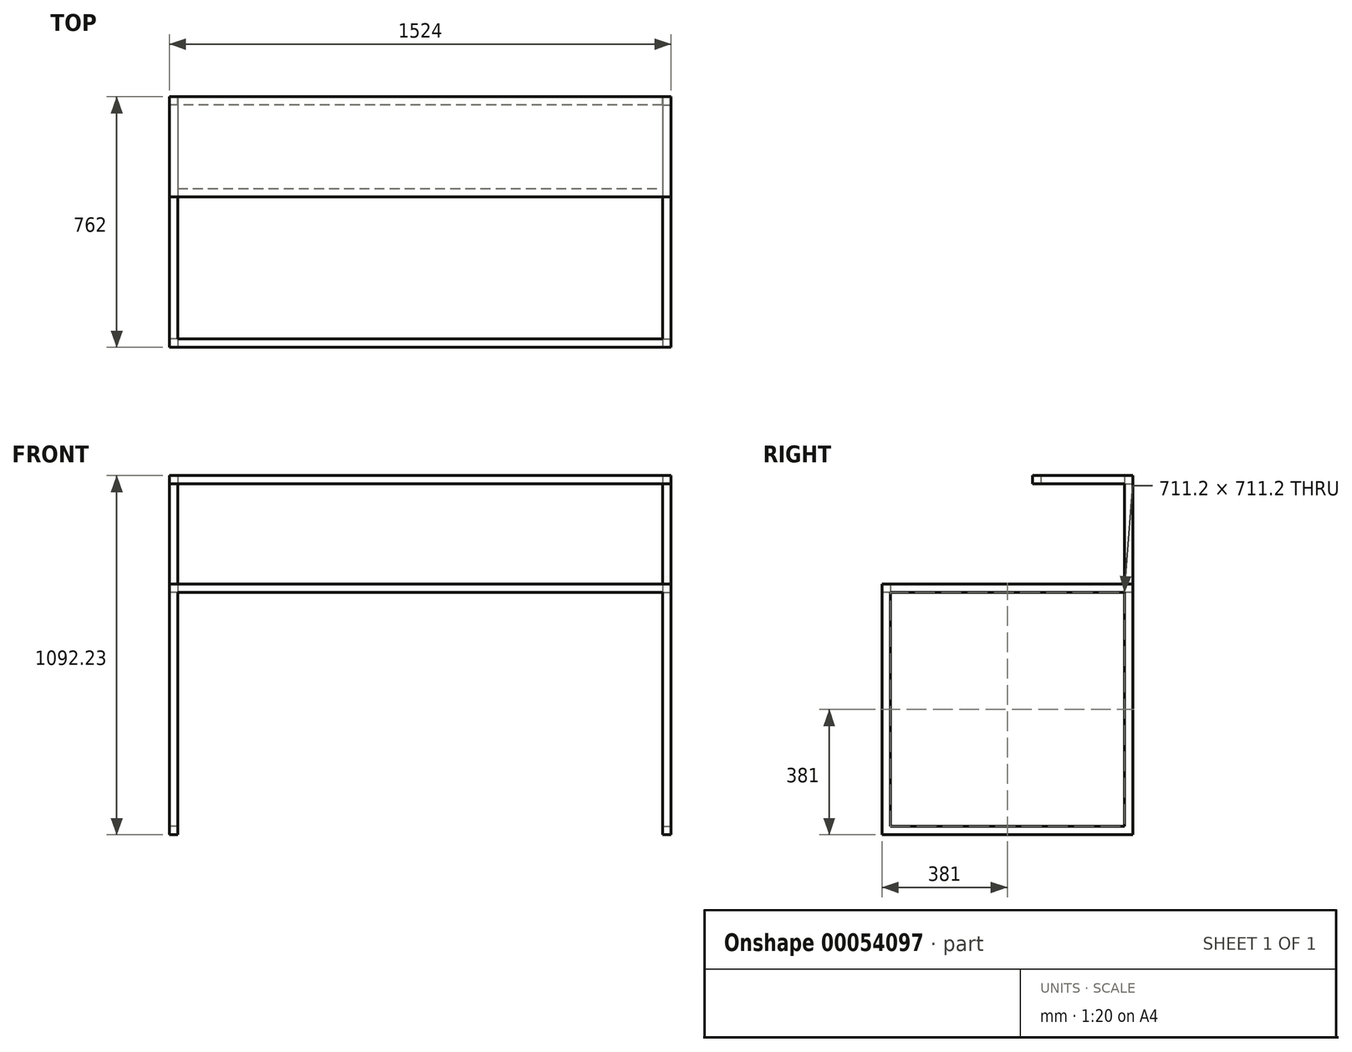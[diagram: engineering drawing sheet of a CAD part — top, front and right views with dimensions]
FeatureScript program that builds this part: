
annotation { "Feature Type Name" : "Feature", "Feature Type Description" : "" }
export const myFeature = defineFeature(function(context is Context, id is Id, definition is map)
    precondition{}
    {
        {
            var Q0;
            Q0=qCreatedBy(makeId("Top.planeOp"),FACE);
            var sketch = newSketch(context, id + "F0", { "sketchPlane" : qUnion([Q0])});
            skLineSegment(sketch, "E0.rect.bottom", {"start": v(762, 381) * mm, "end": v(-762, 381) * mm});
            skLineSegment(sketch, "E0.rect.top", {"start": v(762, -381) * mm, "end": v(-762, -381) * mm});
            skLineSegment(sketch, "E0.rect.left", {"start": v(762, 381) * mm, "end": v(762, -381) * mm});
            skLineSegment(sketch, "E0.rect.right", {"start": v(-762, 381) * mm, "end": v(-762, -381) * mm});
            skPoint(sketch, "E0.rect.middle", {"position": v(0, 0) * mm});
            skLineSegment(sketch, "E1.0", {"start": v(736.6, 355.6) * mm, "end": v(-736.6, 355.6) * mm});
            skLineSegment(sketch, "E1.1", {"start": v(736.6, 355.6) * mm, "end": v(736.6, -355.6) * mm});
            skLineSegment(sketch, "E1.2", {"start": v(736.6, -355.6) * mm, "end": v(-736.6, -355.6) * mm});
            skLineSegment(sketch, "E1.3", {"start": v(-736.6, 355.6) * mm, "end": v(-736.6, -355.6) * mm});
            skSolve(sketch);
        }
        {
            var Q0;
            Q0 = qSketchRegion(id + "F0", true);
            extrude(context, id + "F1", {"entities" : qUnion([Q0]), "depth" : 25.4 * mm});
        }
        {
            var Q0;
            Q0=makeQuery(id+"F1.opExtrude","CAP_FACE",FACE,{"disambiguationData":[OSD([sQuery(id+"F0.wireOp",EDGE,"E0.rect.bottom"),sQuery(id+"F0.wireOp",EDGE,"E0.rect.top"),sQuery(id+"F0.wireOp",EDGE,"E0.rect.left"),sQuery(id+"F0.wireOp",EDGE,"E0.rect.right"),sQuery(id+"F0.wireOp",EDGE,"E1.0"),sQuery(id+"F0.wireOp",EDGE,"E1.1"),sQuery(id+"F0.wireOp",EDGE,"E1.2"),sQuery(id+"F0.wireOp",EDGE,"E1.3")])],"isStart":true});
            var sketch = newSketch(context, id + "F2", { "sketchPlane" : qUnion([Q0])});
            skLineSegment(sketch, "E2.bottom", {"start": v(-736.6, 355.6) * mm, "end": v(-762, 355.6) * mm});
            skLineSegment(sketch, "E2.top", {"start": v(-736.6, 381) * mm, "end": v(-762, 381) * mm});
            skLineSegment(sketch, "E2.left", {"start": v(-736.6, 355.6) * mm, "end": v(-736.6, 381) * mm});
            skLineSegment(sketch, "E2.right", {"start": v(-762, 355.6) * mm, "end": v(-762, 381) * mm});
            skLineSegment(sketch, "E3.bottom", {"start": v(-736.6, -355.6) * mm, "end": v(-762, -355.6) * mm});
            skLineSegment(sketch, "E3.top", {"start": v(-736.6, -381) * mm, "end": v(-762, -381) * mm});
            skLineSegment(sketch, "E3.left", {"start": v(-736.6, -355.6) * mm, "end": v(-736.6, -381) * mm});
            skLineSegment(sketch, "E3.right", {"start": v(-762, -355.6) * mm, "end": v(-762, -381) * mm});
            skLineSegment(sketch, "E4.bottom", {"start": v(762, -381) * mm, "end": v(736.6, -381) * mm});
            skLineSegment(sketch, "E4.top", {"start": v(762, -355.6) * mm, "end": v(736.6, -355.6) * mm});
            skLineSegment(sketch, "E4.left", {"start": v(762, -381) * mm, "end": v(762, -355.6) * mm});
            skLineSegment(sketch, "E4.right", {"start": v(736.6, -381) * mm, "end": v(736.6, -355.6) * mm});
            skLineSegment(sketch, "E5.bottom", {"start": v(736.6, 355.6) * mm, "end": v(762, 355.6) * mm});
            skLineSegment(sketch, "E5.top", {"start": v(736.6, 381) * mm, "end": v(762, 381) * mm});
            skLineSegment(sketch, "E5.left", {"start": v(736.6, 355.6) * mm, "end": v(736.6, 381) * mm});
            skLineSegment(sketch, "E5.right", {"start": v(762, 355.6) * mm, "end": v(762, 381) * mm});
            skSolve(sketch);
        }
        {
            var Q0;
            Q0=makeQuery(id+"F2.imprint","IMPRINT",FACE,{"disambiguationData":[TD([[makeQuery(id+"F2.imprint","IMPRINT",EDGE,{"derivedFrom":sQuery(id+"F2.wireOp",EDGE,"E2.bottom")}),-1.0]])]});
            var Q1;
            Q1=makeQuery(id+"F2.imprint","IMPRINT",FACE,{"disambiguationData":[TD([[makeQuery(id+"F2.imprint","IMPRINT",EDGE,{"derivedFrom":sQuery(id+"F2.wireOp",EDGE,"E3.bottom")}),1.0]])]});
            var Q2;
            Q2=makeQuery(id+"F2.imprint","IMPRINT",FACE,{"disambiguationData":[TD([[makeQuery(id+"F2.imprint","IMPRINT",EDGE,{"derivedFrom":sQuery(id+"F2.wireOp",EDGE,"E4.bottom")}),-1.0]])]});
            var Q3;
            Q3=makeQuery(id+"F2.imprint","IMPRINT",FACE,{"disambiguationData":[TD([[makeQuery(id+"F2.imprint","IMPRINT",EDGE,{"derivedFrom":sQuery(id+"F2.wireOp",EDGE,"E5.bottom")}),1.0]])]});
            extrude(context, id + "F3", {"entities" : qUnion([Q0, Q1, Q2, Q3]), "operationType" : NewBodyOperationType.ADD, "depth" : 736.6 * mm});
        }
        {
            var Q0;
            Q0=makeQuery(id+"F1.opExtrude","CAP_FACE",FACE,{"disambiguationData":[OSD([sQuery(id+"F0.wireOp",EDGE,"E0.rect.bottom"),sQuery(id+"F0.wireOp",EDGE,"E0.rect.top"),sQuery(id+"F0.wireOp",EDGE,"E0.rect.left"),sQuery(id+"F0.wireOp",EDGE,"E0.rect.right"),sQuery(id+"F0.wireOp",EDGE,"E1.0"),sQuery(id+"F0.wireOp",EDGE,"E1.1"),sQuery(id+"F0.wireOp",EDGE,"E1.2"),sQuery(id+"F0.wireOp",EDGE,"E1.3")])],"isStart":false});
            var sketch = newSketch(context, id + "F4", { "sketchPlane" : qUnion([Q0])});
            skLineSegment(sketch, "E6.bottom", {"start": v(-736.6, 355.6) * mm, "end": v(-762, 355.6) * mm});
            skLineSegment(sketch, "E6.top", {"start": v(-736.6, 381) * mm, "end": v(-762, 381) * mm});
            skLineSegment(sketch, "E6.left", {"start": v(-736.6, 355.6) * mm, "end": v(-736.6, 381) * mm});
            skLineSegment(sketch, "E6.right", {"start": v(-762, 355.6) * mm, "end": v(-762, 381) * mm});
            skLineSegment(sketch, "E7.bottom", {"start": v(736.6, 355.6) * mm, "end": v(762, 355.6) * mm});
            skLineSegment(sketch, "E7.top", {"start": v(736.6, 381) * mm, "end": v(762, 381) * mm});
            skLineSegment(sketch, "E7.left", {"start": v(736.6, 355.6) * mm, "end": v(736.6, 381) * mm});
            skLineSegment(sketch, "E7.right", {"start": v(762, 355.6) * mm, "end": v(762, 381) * mm});
            skSolve(sketch);
        }
        {
            var Q0;
            Q0=makeQuery(id+"F4.imprint","IMPRINT",FACE,{"disambiguationData":[TD([[makeQuery(id+"F4.imprint","IMPRINT",EDGE,{"derivedFrom":sQuery(id+"F4.wireOp",EDGE,"E7.bottom")}),1.0]])]});
            var Q1;
            Q1=makeQuery(id+"F4.imprint","IMPRINT",FACE,{"disambiguationData":[TD([[makeQuery(id+"F4.imprint","IMPRINT",EDGE,{"derivedFrom":sQuery(id+"F4.wireOp",EDGE,"E6.bottom")}),-1.0]])]});
            var Q2;
            Q2=makeQuery(id+"F4.imprint","IMPRINT",FACE,{"disambiguationData":[TD([[makeQuery(id+"F4.imprint","IMPRINT",EDGE,{"derivedFrom":sQuery(id+"F4.wireOp",EDGE,"a08b17ff-189d-42e0-89d5-0d836113f8d2.bottom")}),-1.0]])]});
            var Q3;
            Q3=makeQuery(id+"F4.imprint","IMPRINT",FACE,{"disambiguationData":[TD([[makeQuery(id+"F4.imprint","IMPRINT",EDGE,{"derivedFrom":sQuery(id+"F4.wireOp",EDGE,"f9240952-c8aa-4458-8341-3ee3489270d4.bottom")}),-1.0]])]});
            extrude(context, id + "F5", {"entities" : qUnion([Q0, Q1, Q2, Q3]), "operationType" : NewBodyOperationType.ADD, "depth" : 304.8 * mm});
        }
        {
            var Q0;
            Q0=makeQuery(id+"F5.opExtrude","CAP_FACE",FACE,{"disambiguationData":[OSD([sQuery(id+"F4.wireOp",EDGE,"E6.bottom"),sQuery(id+"F4.wireOp",EDGE,"E6.top"),sQuery(id+"F4.wireOp",EDGE,"E6.left"),sQuery(id+"F4.wireOp",EDGE,"E6.right")])],"isStart":false});
            var sketch = newSketch(context, id + "F6", { "sketchPlane" : qUnion([Q0])});
            skLineSegment(sketch, "E8.bottom", {"start": v(-762, 381) * mm, "end": v(762, 381) * mm});
            skLineSegment(sketch, "E8.top", {"start": v(-762, 76.2) * mm, "end": v(762, 76.2) * mm});
            skLineSegment(sketch, "E8.left", {"start": v(-762, 381) * mm, "end": v(-762, 76.2) * mm});
            skLineSegment(sketch, "E8.right", {"start": v(762, 381) * mm, "end": v(762, 76.2) * mm});
            skLineSegment(sketch, "E9.bottom", {"start": v(-736.6, 355.6) * mm, "end": v(736.6, 355.6) * mm});
            skLineSegment(sketch, "E9.top", {"start": v(-736.6, 101.6) * mm, "end": v(736.6, 101.6) * mm});
            skLineSegment(sketch, "E9.left", {"start": v(-736.6, 355.6) * mm, "end": v(-736.6, 101.6) * mm});
            skLineSegment(sketch, "E9.right", {"start": v(736.6, 355.6) * mm, "end": v(736.6, 101.6) * mm});
            skSolve(sketch);
        }
        {
            var Q0;
            Q0 = qSketchRegion(id + "F6", true);
            extrude(context, id + "F7", {"entities" : qUnion([Q0]), "operationType" : NewBodyOperationType.ADD, "depth" : 25.4 * mm});
        }
        {
            var Q0;
            Q0=makeQuery(id+"F5.boolean.opBoolean","MERGE",FACE,{"derivedFrom":[makeQuery(id+"F3.boolean.opBoolean","MERGE",FACE,{"derivedFrom":[makeQuery(id+"F1.opExtrude","SWEPT_FACE",FACE,{"disambiguationData":[OSD([sQuery(id+"F0.wireOp",EDGE,"E0.rect.left")])]}),makeQuery(id+"F3.opExtrude","SWEPT_FACE",FACE,{"disambiguationData":[OSD([sQuery(id+"F2.wireOp",EDGE,"E4.left")])]}),makeQuery(id+"F3.opExtrude","SWEPT_FACE",FACE,{"disambiguationData":[OSD([sQuery(id+"F2.wireOp",EDGE,"E5.right")])]})]}),makeQuery(id+"F5.opExtrude","SWEPT_FACE",FACE,{"disambiguationData":[OSD([sQuery(id+"F4.wireOp",EDGE,"E7.right")])]})]});
            var sketch = newSketch(context, id + "F8", { "sketchPlane" : qUnion([Q0])});
            skLineSegment(sketch, "E10.bottom", {"start": v(-381, -736.6) * mm, "end": v(381, -736.6) * mm});
            skLineSegment(sketch, "E10.top", {"start": v(-381, -711.2) * mm, "end": v(381, -711.2) * mm});
            skLineSegment(sketch, "E10.left", {"start": v(-381, -736.6) * mm, "end": v(-381, -711.2) * mm});
            skLineSegment(sketch, "E10.right", {"start": v(381, -736.6) * mm, "end": v(381, -711.2) * mm});
            skSolve(sketch);
        }
        {
            var Q0;
            {var subQ0=sQuery(id+"F8.wireOp",EDGE,"E10.bottom");var subQ1=sQuery(id+"F0.wireOp",EDGE,"E0.rect.left");var subQ2=makeQuery(id+"F3.opExtrude","SWEPT_EDGE",EDGE,{"disambiguationData":[OSD([subQ1,sQuery(id+"F2.wireOp",EDGE,"E4.top"),sQuery(id+"F2.wireOp",EDGE,"E4.left")])]});var subQ3=makeQuery(id+"F8.imprint","INTERSECT",VERTEX,{"derivedFrom":[subQ2,subQ0]});var subQ4=makeQuery(id+"F3.opExtrude","SWEPT_EDGE",EDGE,{"disambiguationData":[OSD([subQ1,sQuery(id+"F2.wireOp",EDGE,"E5.bottom"),sQuery(id+"F2.wireOp",EDGE,"E5.right")])]});var subQ5=makeQuery(id+"F8.imprint","INTERSECT",VERTEX,{"derivedFrom":[subQ4,subQ0]});Q0=makeQuery(id+"F8.imprint","IMPRINT",FACE,{"disambiguationData":[TD([[makeQuery(id+"F8.imprint","IMPRINT",EDGE,{"disambiguationData":[TD([[subQ3,1.0],[subQ5,-1.0]])],"derivedFrom":subQ0}),1.0]])]});}
            extrude(context, id + "F9", {"entities" : qUnion([Q0]), "operationType" : NewBodyOperationType.ADD, "oppositeDirection" : true, "depth" : 25.4 * mm});
        }
        {
            var Q0;
            Q0=makeQuery(id+"F7.boolean.opBoolean","MERGE",FACE,{"derivedFrom":[makeQuery(id+"F5.boolean.opBoolean","MERGE",FACE,{"derivedFrom":[makeQuery(id+"F3.boolean.opBoolean","MERGE",FACE,{"derivedFrom":[makeQuery(id+"F1.opExtrude","SWEPT_FACE",FACE,{"disambiguationData":[OSD([sQuery(id+"F0.wireOp",EDGE,"E0.rect.right")])]}),makeQuery(id+"F3.opExtrude","SWEPT_FACE",FACE,{"disambiguationData":[OSD([sQuery(id+"F2.wireOp",EDGE,"E2.right")])]}),makeQuery(id+"F3.opExtrude","SWEPT_FACE",FACE,{"disambiguationData":[OSD([sQuery(id+"F2.wireOp",EDGE,"E3.right")])]})]}),makeQuery(id+"F5.opExtrude","SWEPT_FACE",FACE,{"disambiguationData":[OSD([sQuery(id+"F4.wireOp",EDGE,"E6.right")])]})]}),makeQuery(id+"F7.opExtrude","SWEPT_FACE",FACE,{"disambiguationData":[OSD([sQuery(id+"F6.wireOp",EDGE,"E8.left")])]})]});
            var sketch = newSketch(context, id + "F10", { "sketchPlane" : qUnion([Q0])});
            skLineSegment(sketch, "E11.bottom", {"start": v(-381, -736.6) * mm, "end": v(381, -736.6) * mm});
            skLineSegment(sketch, "E11.top", {"start": v(-381, -711.2) * mm, "end": v(381, -711.2) * mm});
            skLineSegment(sketch, "E11.left", {"start": v(-381, -736.6) * mm, "end": v(-381, -711.2) * mm});
            skLineSegment(sketch, "E11.right", {"start": v(381, -736.6) * mm, "end": v(381, -711.2) * mm});
            skSolve(sketch);
        }
        {
            var Q0;
            {var subQ0=sQuery(id+"F10.wireOp",EDGE,"E11.bottom");var subQ1=sQuery(id+"F0.wireOp",EDGE,"E0.rect.right");var subQ2=makeQuery(id+"F3.opExtrude","SWEPT_EDGE",EDGE,{"disambiguationData":[OSD([subQ1,sQuery(id+"F2.wireOp",EDGE,"E2.bottom"),sQuery(id+"F2.wireOp",EDGE,"E2.right")])]});var subQ3=makeQuery(id+"F10.imprint","INTERSECT",VERTEX,{"derivedFrom":[subQ2,subQ0]});Q0=makeQuery(id+"F10.imprint","IMPRINT",FACE,{"disambiguationData":[TD([[makeQuery(id+"F10.imprint","IMPRINT",EDGE,{"disambiguationData":[TD([[subQ3,1.0]])],"derivedFrom":subQ0}),1.0]])]});}
            extrude(context, id + "F11", {"entities" : qUnion([Q0]), "operationType" : NewBodyOperationType.ADD, "oppositeDirection" : true, "depth" : 25.4 * mm});
        }
        {
            var Q0;
            {var subQ0=sQuery(id+"F0.wireOp",EDGE,"E1.3");var subQ1=sQuery(id+"F0.wireOp",EDGE,"E1.2");var subQ2=sQuery(id+"F0.wireOp",EDGE,"E1.1");var subQ3=sQuery(id+"F0.wireOp",EDGE,"E1.0");var subQ4=sQuery(id+"F0.wireOp",EDGE,"E0.rect.right");var subQ5=sQuery(id+"F0.wireOp",EDGE,"E0.rect.left");var subQ6=sQuery(id+"F0.wireOp",EDGE,"E0.rect.top");var subQ7=makeQuery(id+"F1.opExtrude","CAP_FACE",FACE,{"disambiguationData":[OSD([sQuery(id+"F0.wireOp",EDGE,"E0.rect.bottom"),subQ6,subQ5,subQ4,subQ3,subQ2,subQ1,subQ0])],"isStart":false});Q0=makeQuery(id+"F5.boolean.opBoolean","SPLIT",FACE,{"disambiguationData":[TD([makeQuery(id+"F1.opExtrude","SWEPT_FACE",FACE,{"disambiguationData":[OSD([subQ6])]})])],"derivedFrom":subQ7});}
            var sketch = newSketch(context, id + "F12", { "sketchPlane" : qUnion([Q0])});
            skLineSegment(sketch, "E12.bottom", {"start": v(-762, -381) * mm, "end": v(762, -381) * mm});
            skLineSegment(sketch, "E12.top", {"start": v(-762, 381) * mm, "end": v(762, 381) * mm});
            skLineSegment(sketch, "E12.left", {"start": v(-762, -381) * mm, "end": v(-762, 381) * mm});
            skLineSegment(sketch, "E12.right", {"start": v(762, -381) * mm, "end": v(762, 381) * mm});
            skLineSegment(sketch, "E13.bottom", {"start": v(762, 381) * mm, "end": v(736.6, 381) * mm});
            skLineSegment(sketch, "E13.top", {"start": v(762, 355.6) * mm, "end": v(736.6, 355.6) * mm});
            skLineSegment(sketch, "E13.left", {"start": v(762, 381) * mm, "end": v(762, 355.6) * mm});
            skLineSegment(sketch, "E13.right", {"start": v(736.6, 381) * mm, "end": v(736.6, 355.6) * mm});
            skLineSegment(sketch, "E14.bottom", {"start": v(-762, 381) * mm, "end": v(-736.6, 381) * mm});
            skLineSegment(sketch, "E14.top", {"start": v(-762, 355.6) * mm, "end": v(-736.6, 355.6) * mm});
            skLineSegment(sketch, "E14.left", {"start": v(-762, 381) * mm, "end": v(-762, 355.6) * mm});
            skLineSegment(sketch, "E14.right", {"start": v(-736.6, 381) * mm, "end": v(-736.6, 355.6) * mm});
            skSolve(sketch);
        }
        {
            var Q0;
            Q0=makeQuery(id+"F12.imprint","IMPRINT",FACE,{"disambiguationData":[TD([[makeQuery(id+"F12.imprint","IMPRINT",EDGE,{"derivedFrom":sQuery(id+"F12.wireOp",EDGE,"E12.top")}),-1.0]])]});
            var Q1;
            Q1=makeQuery(id+"F12.imprint","IMPRINT",FACE,{"disambiguationData":[TD([[makeQuery(id+"F12.imprint","IMPRINT",EDGE,{"derivedFrom":sQuery(id+"F12.wireOp",EDGE,"E12.bottom")}),-1.0]])]});
            extrude(context, id + "F13", {"entities" : qUnion([Q0, Q1]), "depth" : 3 / 101.6 * mm});
        }
        {
            var Q0;
            Q0=makeQuery(id+"F7.opExtrude","CAP_FACE",FACE,{"disambiguationData":[OSD([sQuery(id+"F6.wireOp",EDGE,"E8.bottom"),sQuery(id+"F6.wireOp",EDGE,"E8.top"),sQuery(id+"F6.wireOp",EDGE,"E8.left"),sQuery(id+"F6.wireOp",EDGE,"E8.right"),sQuery(id+"F6.wireOp",EDGE,"E9.bottom"),sQuery(id+"F6.wireOp",EDGE,"E9.top"),sQuery(id+"F6.wireOp",EDGE,"E9.left"),sQuery(id+"F6.wireOp",EDGE,"E9.right")])],"isStart":false});
            var sketch = newSketch(context, id + "F14", { "sketchPlane" : qUnion([Q0])});
            skLineSegment(sketch, "E15.bottom", {"start": v(-762, 381) * mm, "end": v(762, 381) * mm});
            skLineSegment(sketch, "E15.top", {"start": v(-762, 76.2) * mm, "end": v(762, 76.2) * mm});
            skLineSegment(sketch, "E15.left", {"start": v(-762, 381) * mm, "end": v(-762, 76.2) * mm});
            skLineSegment(sketch, "E15.right", {"start": v(762, 381) * mm, "end": v(762, 76.2) * mm});
            skSolve(sketch);
        }
        {
            var Q0;
            Q0=makeQuery(id+"F14.imprint","IMPRINT",FACE,{"disambiguationData":[TD([[makeQuery(id+"F14.imprint","IMPRINT",EDGE,{"derivedFrom":sQuery(id+"F14.wireOp",EDGE,"E15.bottom")}),1.0]])]});
            var Q1;
            Q1=makeQuery(id+"F14.imprint","IMPRINT",FACE,{"disambiguationData":[TD([[makeQuery(id+"F14.imprint","IMPRINT",EDGE,{"derivedFrom":makeQuery(id+"F7.opExtrude","CAP_EDGE",EDGE,{"disambiguationData":[OSD([sQuery(id+"F6.wireOp",EDGE,"E9.bottom")])],"isStart":false})}),-1.0]])]});
            extrude(context, id + "F15", {"entities" : qUnion([Q0, Q1]), "depth" : 3 / 101.6 * mm});
        }
    });
